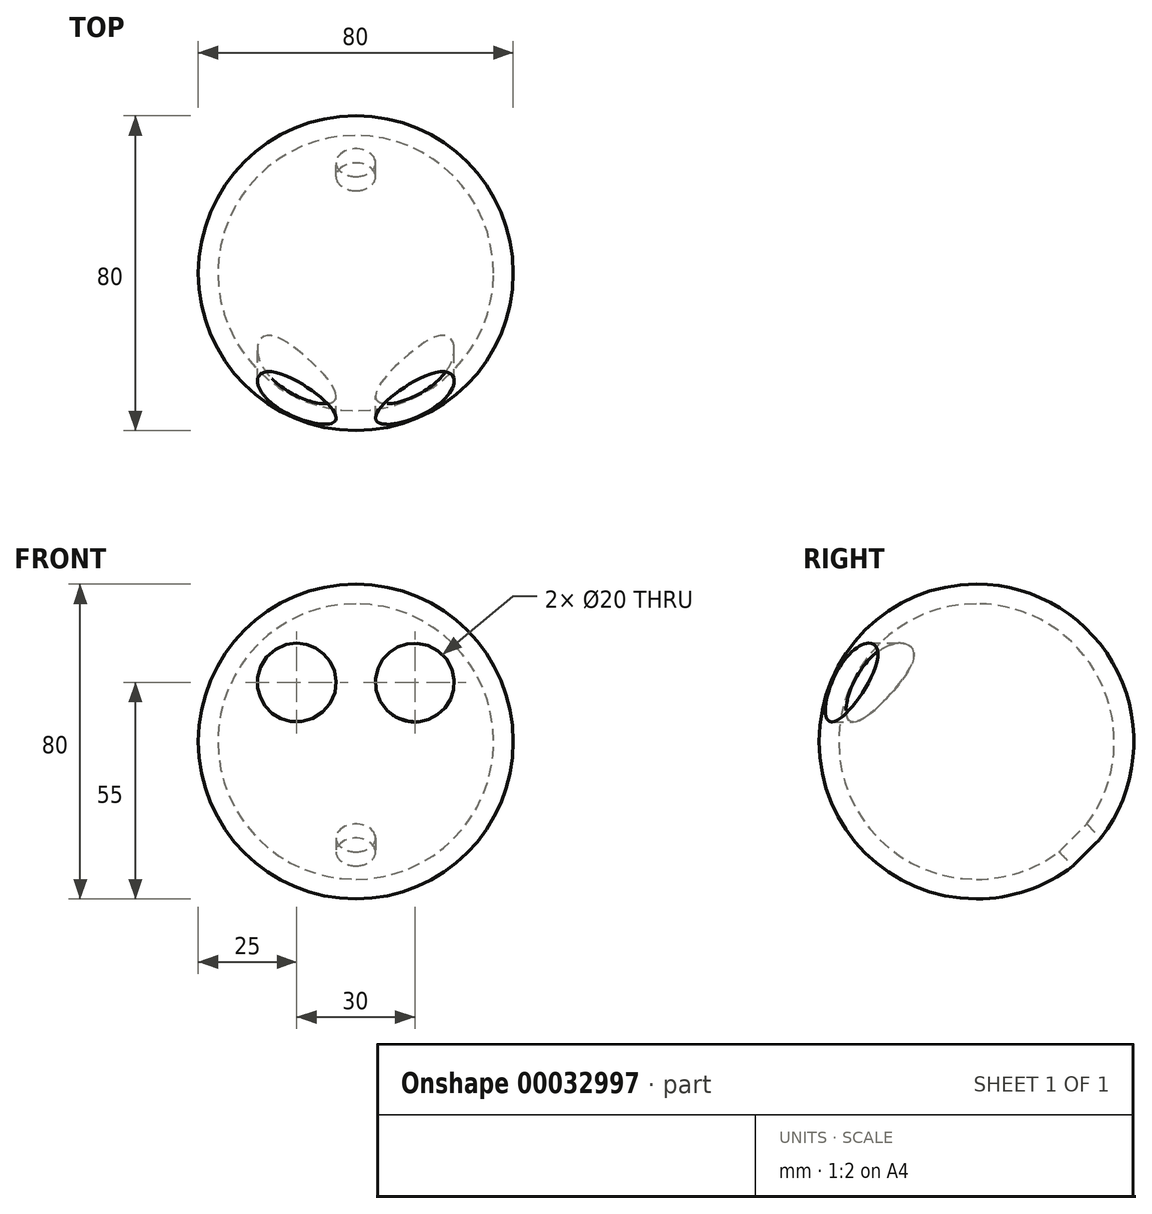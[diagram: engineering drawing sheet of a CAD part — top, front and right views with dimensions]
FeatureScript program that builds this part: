
annotation { "Feature Type Name" : "Feature", "Feature Type Description" : "" }
export const myFeature = defineFeature(function(context is Context, id is Id, definition is map)
    precondition{}
    {
        {
            var Q0;
            Q0=qCreatedBy(makeId("Right.planeOp"),FACE);
            var sketch = newSketch(context, id + "F0", { "sketchPlane" : qUnion([Q0])});
            skArc(sketch, "E0", {"start": v(0, -40) * mm, "mid": v(40, 0) * mm, "end": v(0, 40) * mm});
            skLineSegment(sketch, "E1", {"start": v(0, 40) * mm, "end": v(0, -40) * mm});
            skSolve(sketch);
        }
        {
            var Q0;
            Q0 = qSketchRegion(id + "F0", true);
            var Q1;
            Q1=sQuery(id+"F0.wireOp",EDGE,"E1");
            revolve(context, id + "F1", {"entities" : qUnion([Q0]), "axis" : qUnion([Q1]), "revolveType" : RevolveType.FULL});
        }
        {
            var Q0;
            Q0=qCreatedBy(makeId("Right.planeOp"),FACE);
            var sketch = newSketch(context, id + "F2", { "sketchPlane" : qUnion([Q0])});
            skLineSegment(sketch, "E2", {"start": v(0, 0) * mm, "end": v(17.68, -17.68) * mm, "construction": true});
            skLineSegment(sketch, "E3", {"start": v(17.68, -17.68) * mm, "end": v(14.14, -21.21) * mm});
            skLineSegment(sketch, "E4", {"start": v(14.14, -21.21) * mm, "end": v(31.82, -38.9) * mm});
            skLineSegment(sketch, "E5", {"start": v(31.82, -38.9) * mm, "end": v(35.36, -35.36) * mm});
            skLineSegment(sketch, "E6", {"start": v(17.68, -17.68) * mm, "end": v(35.36, -35.36) * mm});
            skLineSegment(sketch, "E7", {"start": v(0, 0) * mm, "end": v(40, 0) * mm, "construction": true});
            skSolve(sketch);
        }
        {
            var Q0;
            Q0 = qSketchRegion(id + "F2", true);
            var Q1;
            Q1=sQuery(id+"F2.wireOp",EDGE,"E6");
            revolve(context, id + "F3", {"operationType" : NewBodyOperationType.REMOVE, "entities" : qUnion([Q0]), "axis" : qUnion([Q1]), "revolveType" : RevolveType.FULL, "oppositeDirection" : true});
        }
        {
            var Q0;
            Q0=makeQuery(id+"F3.boolean.opBoolean","COPY",FACE,{"derivedFrom":makeQuery(id+"F3.opRevolve","SWEPT_FACE",FACE,{"disambiguationData":[OSD([sQuery(id+"F2.wireOp",EDGE,"E4")])]})});
            var Q1;
            Q1=makeQuery(id+"F3.boolean.opBoolean","COPY",FACE,{"derivedFrom":makeQuery(id+"F3.opRevolve","SWEPT_FACE",FACE,{"disambiguationData":[OSD([sQuery(id+"F2.wireOp",EDGE,"E3")])]})});
            shell(context, id + "F4", {"entities" : qUnion([Q0, Q1]), "thickness" : 5 * mm});
        }
        {
            var Q0;
            Q0=qCreatedBy(makeId("Front.planeOp"),FACE);
            var sketch = newSketch(context, id + "F5", { "sketchPlane" : qUnion([Q0])});
            skCircle(sketch, "E8", {"center": v(15, 15) * mm, "radius": 10 * mm});
            skLineSegment(sketch, "E9", {"start": v(50, 0) * mm, "end": v(0, 0) * mm, "construction": true});
            skLineSegment(sketch, "E10", {"start": v(0, 0) * mm, "end": v(0, -50) * mm, "construction": true});
            skLineSegment(sketch, "E11", {"start": v(15, 15) * mm, "end": v(15, -15) * mm, "construction": true});
            skSolve(sketch);
        }
        {
            var Q0;
            Q0 = qSketchRegion(id + "F5", true);
            extrude(context, id + "F6", {"entities" : qUnion([Q0]), "endBound" : BoundingType.THROUGH_ALL, "depth" : 25 * mm});
        }
        {
            var Q0;
            Q0=makeQuery(id+"F6.opExtrude","SWEPT_BODY",BODY,{"disambiguationData":[OSD([sQuery(id+"F5.wireOp",EDGE,"E8")])]});
            var Q1;
            Q1=qCreatedBy(makeId("Right.planeOp"),FACE);
            mirror(context, id + "F7", {"entities" : qUnion([Q0]), "mirrorPlane" : qUnion([Q1])});
        }
        {
            var Q0;
            Q0=makeQuery(id+"F6.opExtrude","SWEPT_BODY",BODY,{"disambiguationData":[OSD([sQuery(id+"F5.wireOp",EDGE,"E8")])]});
            var Q1;
            Q1=makeQuery(id+"F7.opPattern","COPY",BODY,{"derivedFrom":makeQuery(id+"F6.opExtrude","SWEPT_BODY",BODY,{"disambiguationData":[OSD([sQuery(id+"F5.wireOp",EDGE,"E8")])]}),"instanceName":"1"});
            var Q2;
            Q2=makeQuery(id+"F1.opRevolve","SWEPT_BODY",BODY,{"disambiguationData":[OSD([sQuery(id+"F0.wireOp",EDGE,"E0"),sQuery(id+"F0.wireOp",EDGE,"E1")])]});
            booleanBodies(context, id + "F8", {"operationType" : BooleanOperationType.SUBTRACTION, "tools" : qUnion([Q0, Q1]), "targets" : qUnion([Q2])});
        }
    });
